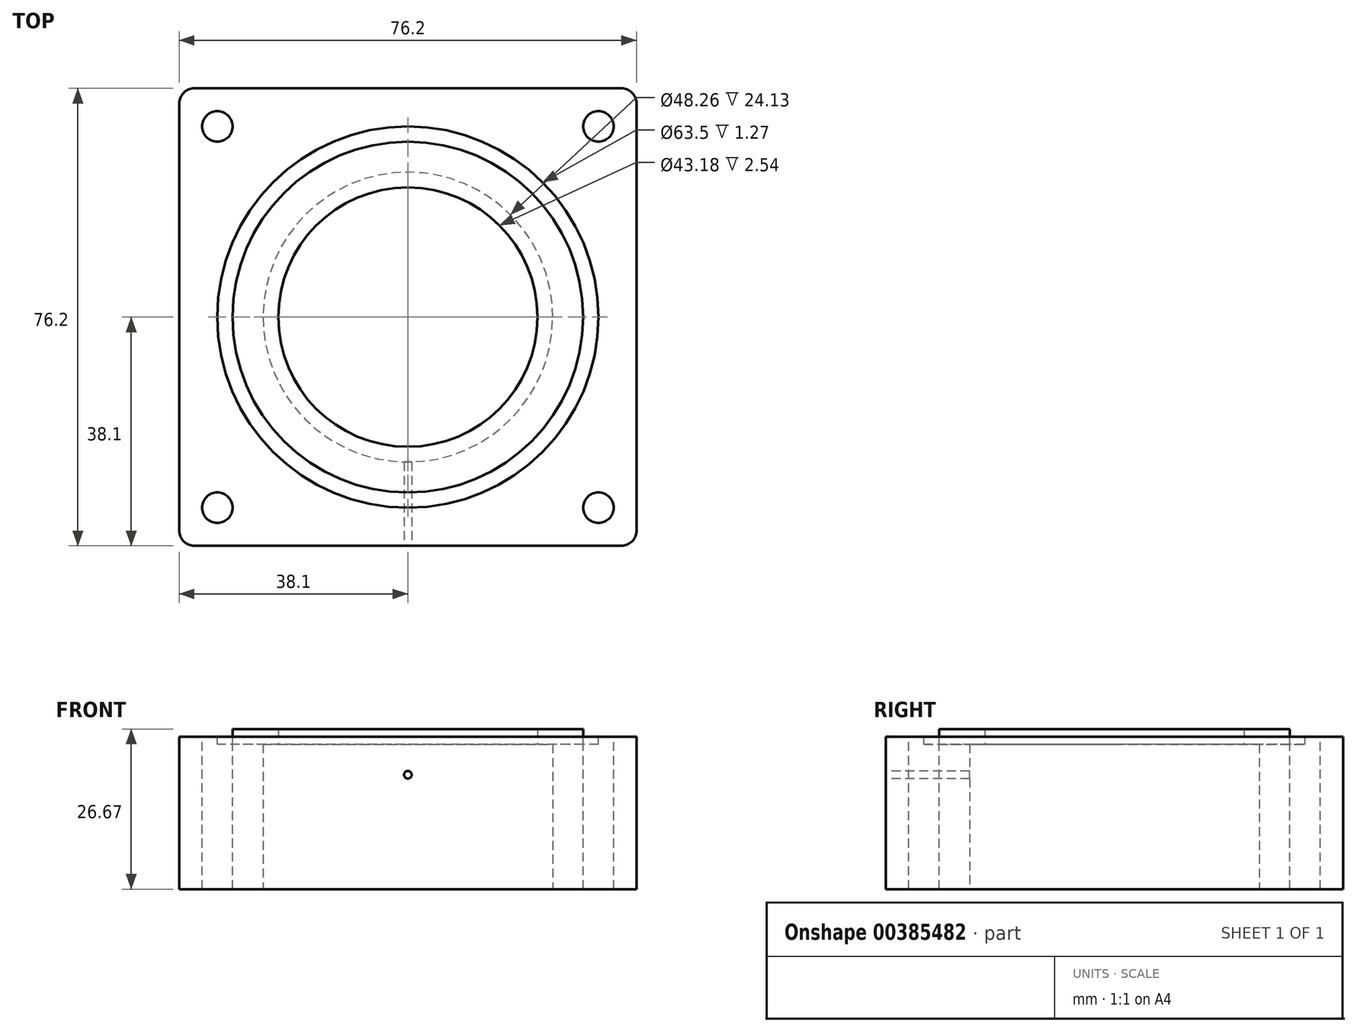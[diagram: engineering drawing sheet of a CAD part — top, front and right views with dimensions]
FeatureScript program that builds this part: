
annotation { "Feature Type Name" : "Feature", "Feature Type Description" : "" }
export const myFeature = defineFeature(function(context is Context, id is Id, definition is map)
    precondition{}
    {
        {
            var Q0;
            Q0=qCreatedBy(makeId("Top.planeOp"),FACE);
            var sketch = newSketch(context, id + "F0", { "sketchPlane" : qUnion([Q0])});
            skLineSegment(sketch, "E0.bottom", {"start": v(-38.1, 38.1) * mm, "end": v(38.1, 38.1) * mm});
            skLineSegment(sketch, "E0.top", {"start": v(-38.1, -38.1) * mm, "end": v(38.1, -38.1) * mm});
            skLineSegment(sketch, "E0.left", {"start": v(-38.1, 38.1) * mm, "end": v(-38.1, -38.1) * mm});
            skLineSegment(sketch, "E0.right", {"start": v(38.1, 38.1) * mm, "end": v(38.1, -38.1) * mm});
            skSolve(sketch);
        }
        {
            var Q0;
            Q0=makeQuery(id+"F0.imprint","IMPRINT",FACE,{"disambiguationData":[TD([[makeQuery(id+"F0.imprint","IMPRINT",EDGE,{"derivedFrom":sQuery(id+"F0.wireOp",EDGE,"E0.bottom")}),-1.0]])]});
            extrude(context, id + "F1", {"entities" : qUnion([Q0]), "depth" : 25.4 * mm});
        }
        {
            var Q0;
            Q0=makeQuery(id+"F1.opExtrude","SWEPT_EDGE",EDGE,{"disambiguationData":[OSD([sQuery(id+"F0.wireOp",EDGE,"E0.top"),sQuery(id+"F0.wireOp",EDGE,"E0.right")])]});
            var Q1;
            Q1=makeQuery(id+"F1.opExtrude","SWEPT_EDGE",EDGE,{"disambiguationData":[OSD([sQuery(id+"F0.wireOp",EDGE,"E0.bottom"),sQuery(id+"F0.wireOp",EDGE,"E0.right")])]});
            var Q2;
            Q2=makeQuery(id+"F1.opExtrude","SWEPT_EDGE",EDGE,{"disambiguationData":[OSD([sQuery(id+"F0.wireOp",EDGE,"E0.top"),sQuery(id+"F0.wireOp",EDGE,"E0.left")])]});
            var Q3;
            Q3=makeQuery(id+"F1.opExtrude","SWEPT_EDGE",EDGE,{"disambiguationData":[OSD([sQuery(id+"F0.wireOp",EDGE,"E0.bottom"),sQuery(id+"F0.wireOp",EDGE,"E0.left")])]});
            fillet(context, id + "F2", {"entities" : qUnion([Q0, Q1, Q2, Q3]), "radius" : 2.54 * mm, "tangentPropagation" : true, "allowEdgeOverflow" : false});
        }
        {
            var Q0;
            Q0=makeQuery(id+"F1.opExtrude","CAP_FACE",FACE,{"disambiguationData":[OSD([sQuery(id+"F0.wireOp",EDGE,"E0.bottom"),sQuery(id+"F0.wireOp",EDGE,"E0.top"),sQuery(id+"F0.wireOp",EDGE,"E0.left"),sQuery(id+"F0.wireOp",EDGE,"E0.right")])],"isStart":false});
            var sketch = newSketch(context, id + "F3", { "sketchPlane" : qUnion([Q0])});
            skCircle(sketch, "E1", {"center": v(0, 0) * mm, "radius": 31.75 * mm});
            skCircle(sketch, "E2", {"center": v(0, 0) * mm, "radius": 29.21 * mm});
            skPoint(sketch, "E3", {"position": v(-31.75, 31.75) * mm});
            skPoint(sketch, "E4", {"position": v(31.75, 31.75) * mm});
            skPoint(sketch, "E5", {"position": v(31.75, -31.75) * mm});
            skPoint(sketch, "E6", {"position": v(-31.75, -31.75) * mm});
            skSolve(sketch);
        }
        {
            var Q0;
            Q0=makeQuery(id+"F3.imprint","IMPRINT",FACE,{"disambiguationData":[TD([[makeQuery(id+"F3.imprint","IMPRINT",EDGE,{"derivedFrom":sQuery(id+"F3.wireOp",EDGE,"E1")}),1.0]])]});
            extrude(context, id + "F4", {"entities" : qUnion([Q0]), "operationType" : NewBodyOperationType.REMOVE, "oppositeDirection" : true, "depth" : 1.27 * mm});
        }
        {
            var Q0;
            Q0=sQuery(id+"F3.wireOp",VERTEX,"E3");
            var Q1;
            Q1=sQuery(id+"F3.wireOp",VERTEX,"E4");
            var Q2;
            Q2=sQuery(id+"F3.wireOp",VERTEX,"E5");
            var Q3;
            Q3=sQuery(id+"F3.wireOp",VERTEX,"E6");
            var Q4;
            Q4=makeQuery(id+"F1.opExtrude","SWEPT_BODY",BODY,{"disambiguationData":[OSD([sQuery(id+"F0.wireOp",EDGE,"E0.bottom"),sQuery(id+"F0.wireOp",EDGE,"E0.top"),sQuery(id+"F0.wireOp",EDGE,"E0.left"),sQuery(id+"F0.wireOp",EDGE,"E0.right")])]});
            hole(context, id + "F5", {"style" : HoleStyle.SIMPLE, "endStyle" : HoleEndStyle.THROUGH, "holeDiameter" : 5.08 * mm, "isTappedThrough" : true, "tappedDepth" : 12.7 * mm, "tapClearance" : 3, "locations" : qUnion([Q0, Q1, Q2, Q3]), "scope" : qUnion([Q4])});
        }
        {
            var Q0;
            Q0=makeQuery(id+"F4.boolean.opBoolean","SPLIT",FACE,{"disambiguationData":[TD([makeQuery(id+"F4.opExtrude","SWEPT_FACE",FACE,{"disambiguationData":[OSD([sQuery(id+"F3.wireOp",EDGE,"E2")])]})])],"derivedFrom":makeQuery(id+"F1.opExtrude","CAP_FACE",FACE,{"disambiguationData":[OSD([sQuery(id+"F0.wireOp",EDGE,"E0.bottom"),sQuery(id+"F0.wireOp",EDGE,"E0.top"),sQuery(id+"F0.wireOp",EDGE,"E0.left"),sQuery(id+"F0.wireOp",EDGE,"E0.right")])],"isStart":false})});
            extrude(context, id + "F6", {"entities" : qUnion([Q0]), "operationType" : NewBodyOperationType.ADD, "depth" : 1.27 * mm});
        }
        {
            var Q0;
            Q0=makeQuery(id+"F1.opExtrude","CAP_FACE",FACE,{"disambiguationData":[OSD([sQuery(id+"F0.wireOp",EDGE,"E0.bottom"),sQuery(id+"F0.wireOp",EDGE,"E0.top"),sQuery(id+"F0.wireOp",EDGE,"E0.left"),sQuery(id+"F0.wireOp",EDGE,"E0.right")])],"isStart":true});
            var sketch = newSketch(context, id + "F7", { "sketchPlane" : qUnion([Q0])});
            skCircle(sketch, "E7", {"center": v(0, 0) * mm, "radius": 24.13 * mm});
            skSolve(sketch);
        }
        {
            var Q0;
            Q0=makeQuery(id+"F7.imprint","IMPRINT",FACE,{"disambiguationData":[TD([[makeQuery(id+"F7.imprint","IMPRINT",EDGE,{"derivedFrom":sQuery(id+"F7.wireOp",EDGE,"E7")}),1.0]])]});
            extrude(context, id + "F8", {"entities" : qUnion([Q0]), "operationType" : NewBodyOperationType.REMOVE, "oppositeDirection" : true, "depth" : 24.13 * mm});
        }
        {
            var Q0;
            Q0=sQuery(id+"F7.wireOp",VERTEX,"E7.center");
            var Q1;
            Q1=makeQuery(id+"F1.opExtrude","SWEPT_BODY",BODY,{"disambiguationData":[OSD([sQuery(id+"F0.wireOp",EDGE,"E0.bottom"),sQuery(id+"F0.wireOp",EDGE,"E0.top"),sQuery(id+"F0.wireOp",EDGE,"E0.left"),sQuery(id+"F0.wireOp",EDGE,"E0.right")])]});
            hole(context, id + "F9", {"style" : HoleStyle.SIMPLE, "endStyle" : HoleEndStyle.THROUGH, "holeDiameter" : 43.18 * mm, "isTappedThrough" : true, "tappedDepth" : 12.7 * mm, "tapClearance" : 3, "locations" : qUnion([Q0]), "scope" : qUnion([Q1])});
        }
        {
            var Q0;
            Q0=makeQuery(id+"F1.opExtrude","SWEPT_FACE",FACE,{"disambiguationData":[OSD([sQuery(id+"F0.wireOp",EDGE,"E0.top")])]});
            var sketch = newSketch(context, id + "F10", { "sketchPlane" : qUnion([Q0])});
            skPoint(sketch, "E8", {"position": v(0, 19.05) * mm});
            skSolve(sketch);
        }
        {
            var Q0;
            Q0=sQuery(id+"F10.wireOp",VERTEX,"E8");
            var Q1;
            Q1=makeQuery(id+"F1.opExtrude","SWEPT_BODY",BODY,{"disambiguationData":[OSD([sQuery(id+"F0.wireOp",EDGE,"E0.bottom"),sQuery(id+"F0.wireOp",EDGE,"E0.top"),sQuery(id+"F0.wireOp",EDGE,"E0.left"),sQuery(id+"F0.wireOp",EDGE,"E0.right")])]});
            hole(context, id + "F11", {"style" : HoleStyle.SIMPLE, "endStyle" : HoleEndStyle.BLIND, "holeDiameter" : 1.27 * mm, "holeDepth" : 25.4 * mm, "isTappedThrough" : true, "tappedDepth" : 12.7 * mm, "tapClearance" : 3, "locations" : qUnion([Q0]), "scope" : qUnion([Q1])});
        }
    });
